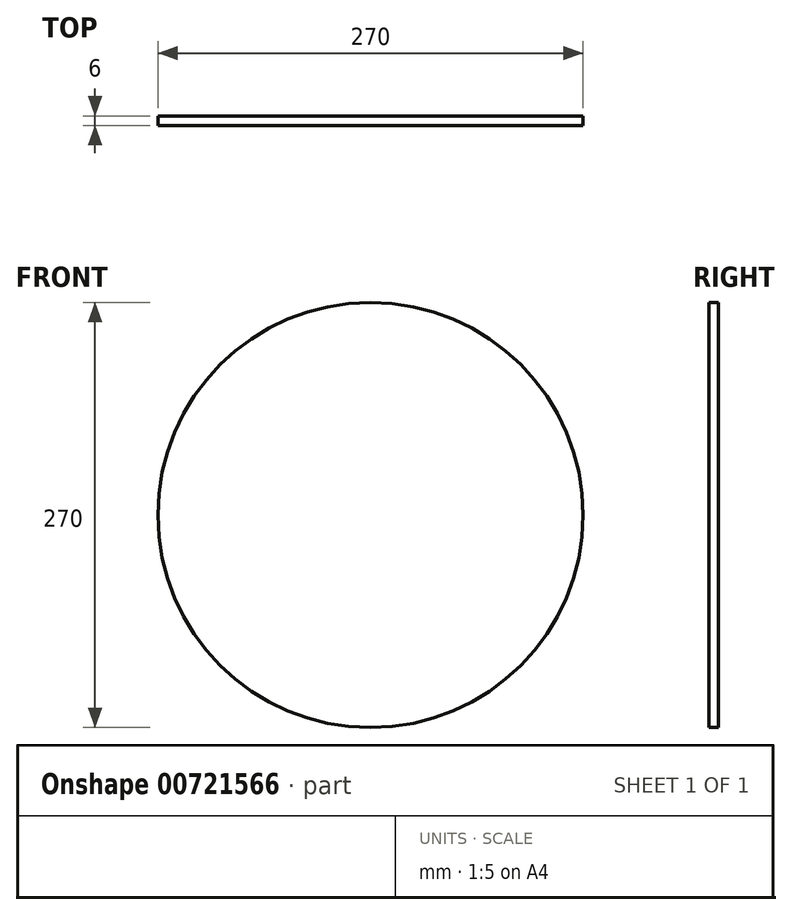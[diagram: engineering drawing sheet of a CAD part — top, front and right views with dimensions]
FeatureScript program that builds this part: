
annotation { "Feature Type Name" : "Feature", "Feature Type Description" : "" }
export const myFeature = defineFeature(function(context is Context, id is Id, definition is map)
    precondition{}
    {
        {
            var Q0;
            Q0=qCreatedBy(makeId("Front.planeOp"),FACE);
            var sketch = newSketch(context, id + "F0", { "sketchPlane" : qUnion([Q0])});
            skCircle(sketch, "E0", {"center": v(0, 0) * mm, "radius": 135 * mm});
            skSolve(sketch);
        }
        {
            var Q0;
            Q0 = qSketchRegion(id + "F0", true);
            extrude(context, id + "F1", {"entities" : qUnion([Q0]), "depth" : 6 * mm, "offsetDistance" : 25 * mm});
        }
    });
